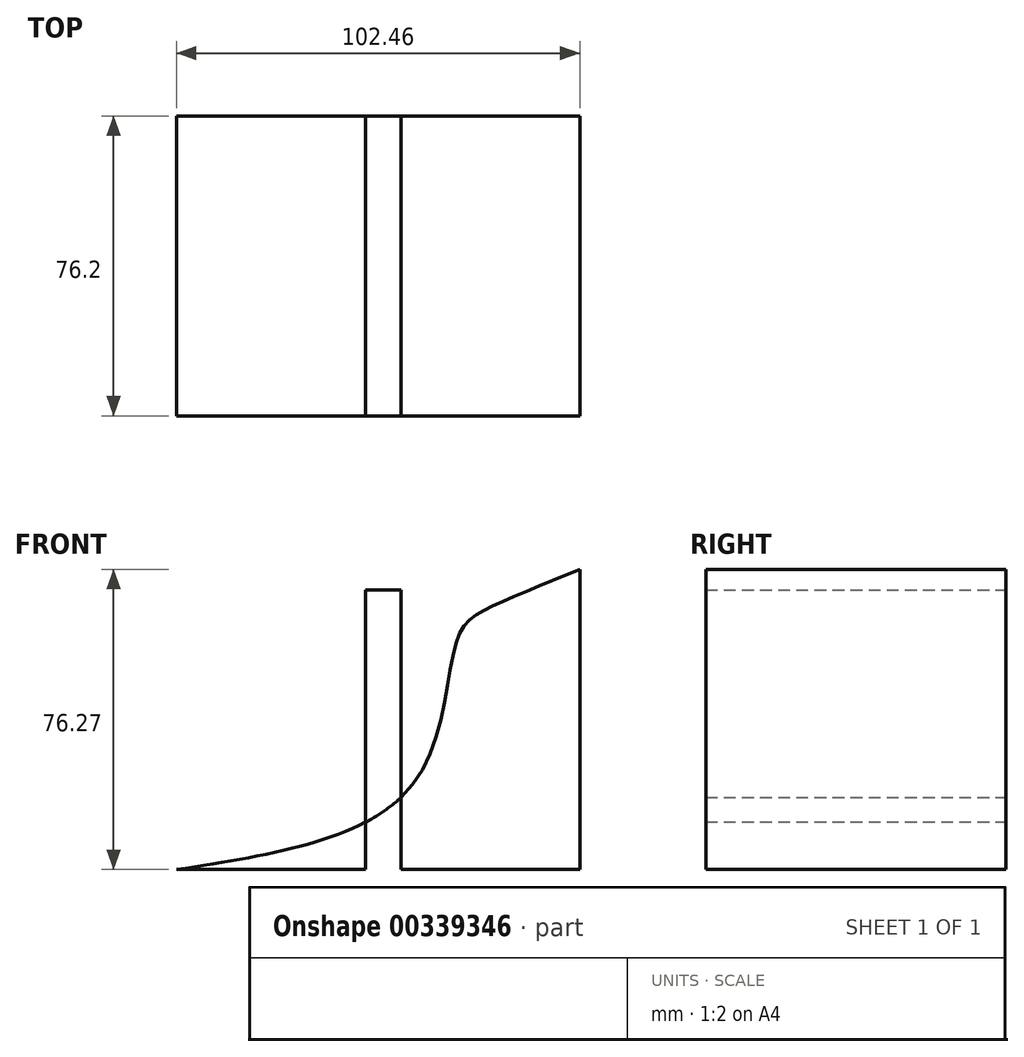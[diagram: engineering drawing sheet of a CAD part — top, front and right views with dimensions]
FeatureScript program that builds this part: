
annotation { "Feature Type Name" : "Feature", "Feature Type Description" : "" }
export const myFeature = defineFeature(function(context is Context, id is Id, definition is map)
    precondition{}
    {
        {
            var Q0;
            Q0=qCreatedBy(makeId("Front.planeOp"),FACE);
            var sketch = newSketch(context, id + "F0", { "sketchPlane" : qUnion([Q0])});
            skLineSegment(sketch, "E0", {"start": v(64.47, 40) * mm, "end": v(64.47, -36.26) * mm});
            skLineSegment(sketch, "E1", {"start": v(64.47, -36.26) * mm, "end": v(-38, -36.26) * mm});
            skFitSpline(sketch, "E2", {"points": [v(64.47, 40) * mm, v(40.87, 29.93) * mm, v(33.39, 22.45) * mm, v(22.45, -14.1) * mm, v(-38, -36.26) * mm], "startDerivative": vector(-119.34, -48.25) * mm, "endDerivative": vector(-209.37, -32.25) * mm});
            skFitSpline(sketch, "E3", {"points": [v(-38, -36.26) * mm, v(-67.35, -36.26) * mm, v(-67.63, -36.26) * mm], "startDerivative": vector(-45.49, 0) * mm, "endDerivative": vector(-1.89, 0) * mm});
            skLineSegment(sketch, "E4.bottom", {"start": v(10.07, 34.82) * mm, "end": v(19, 34.82) * mm});
            skLineSegment(sketch, "E4.top", {"start": v(10.07, -36.26) * mm, "end": v(19, -36.26) * mm});
            skLineSegment(sketch, "E4.left", {"start": v(10.07, 34.82) * mm, "end": v(10.07, -36.26) * mm});
            skLineSegment(sketch, "E4.right", {"start": v(19, 34.82) * mm, "end": v(19, -36.26) * mm});
            skSolve(sketch);
        }
        {
            var Q0;
            {var subQ0=sQuery(id+"F0.wireOp",EDGE,"E2");var subQ1=sQuery(id+"F0.wireOp",EDGE,"E1");var subQ2=makeQuery(id+"F0.imprint","INTERSECT",VERTEX,{"derivedFrom":[subQ1,subQ0]});Q0=makeQuery(id+"F0.imprint","IMPRINT",FACE,{"disambiguationData":[TD([[makeQuery(id+"F0.imprint","IMPRINT",EDGE,{"disambiguationData":[TD([[subQ2,1.0]])],"derivedFrom":subQ0}),1.0]])]});}
            var Q1;
            {var subQ5=sQuery(id+"F0.wireOp",EDGE,"E4.bottom");Q1=makeQuery(id+"F0.imprint","IMPRINT",FACE,{"disambiguationData":[TD([[makeQuery(id+"F0.imprint","IMPRINT",EDGE,{"derivedFrom":subQ5}),-1.0]])]});}
            var Q2;
            {var subQ5=sQuery(id+"F0.wireOp",EDGE,"E4.top");Q2=makeQuery(id+"F0.imprint","IMPRINT",FACE,{"disambiguationData":[TD([[makeQuery(id+"F0.imprint","IMPRINT",EDGE,{"derivedFrom":subQ5}),1.0]])]});}
            var Q3;
            {var subQ0=sQuery(id+"F0.wireOp",EDGE,"E0");Q3=makeQuery(id+"F0.imprint","IMPRINT",FACE,{"disambiguationData":[TD([[makeQuery(id+"F0.imprint","IMPRINT",EDGE,{"derivedFrom":subQ0}),-1.0]])]});}
            extrude(context, id + "F1", {"entities" : qUnion([Q0, Q1, Q2, Q3]), "depth" : 76.2 * mm});
        }
    });
